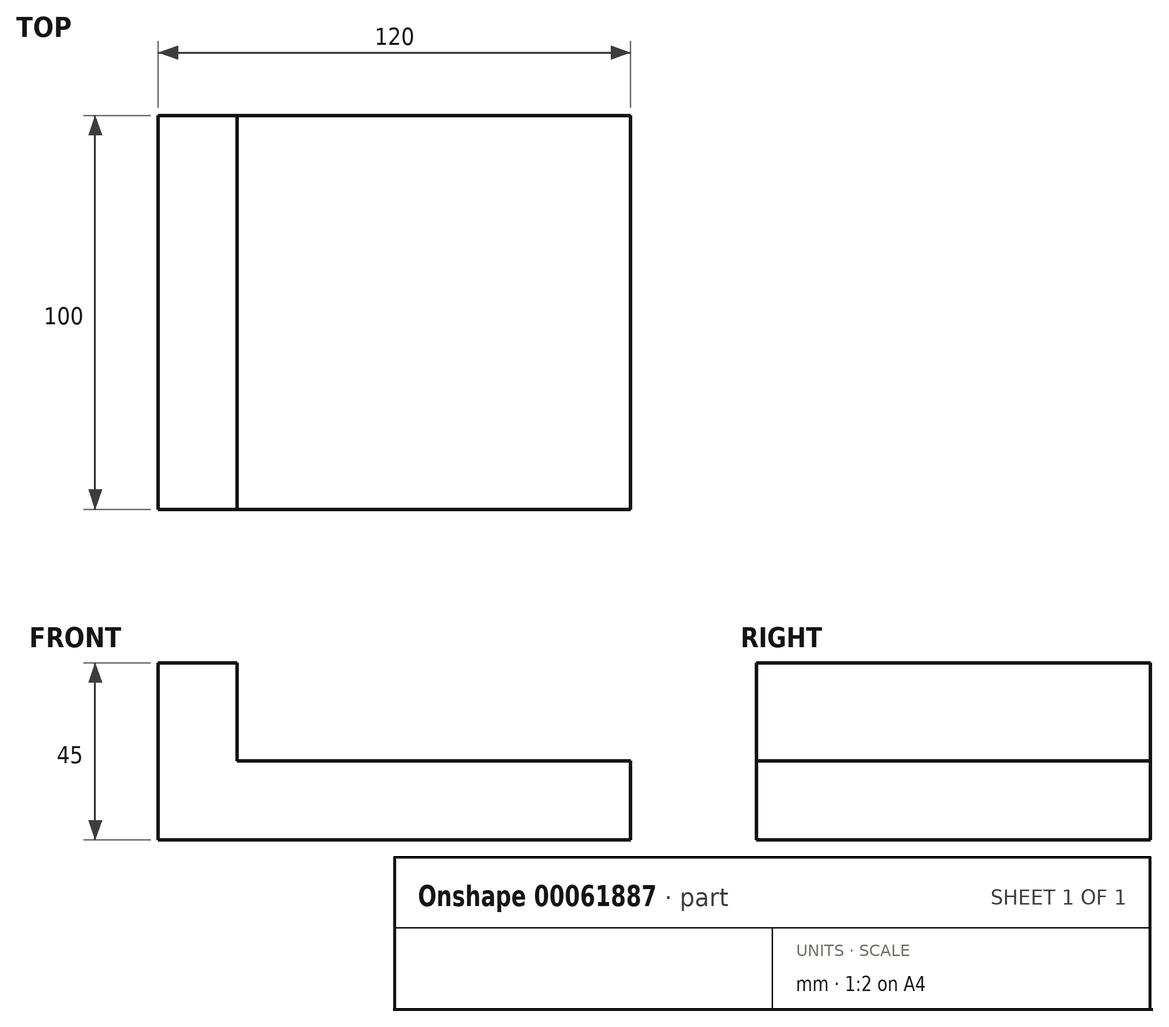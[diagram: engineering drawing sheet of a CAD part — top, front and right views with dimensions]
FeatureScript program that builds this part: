
annotation { "Feature Type Name" : "Feature", "Feature Type Description" : "" }
export const myFeature = defineFeature(function(context is Context, id is Id, definition is map)
    precondition{}
    {
        {
            var Q0;
            Q0=qCreatedBy(makeId("Front.planeOp"),FACE);
            var sketch = newSketch(context, id + "F0", { "sketchPlane" : qUnion([Q0])});
            skLineSegment(sketch, "E0", {"start": v(0, 0) * mm, "end": v(0, 25) * mm});
            skLineSegment(sketch, "E1", {"start": v(0, 0) * mm, "end": v(100, 0) * mm});
            skLineSegment(sketch, "E2", {"start": v(100, 0) * mm, "end": v(100, -20) * mm});
            skLineSegment(sketch, "E3", {"start": v(100, -20) * mm, "end": v(-20, -20) * mm});
            skLineSegment(sketch, "E4", {"start": v(0, 25) * mm, "end": v(-20, 25) * mm});
            skLineSegment(sketch, "E5", {"start": v(-20, 25) * mm, "end": v(-20, -20) * mm});
            skSolve(sketch);
        }
        {
            var Q0;
            Q0=qSketchRegion(id+"F0",true);
            extrude(context, id + "F1", {"entities" : qUnion([Q0]), "endBound" : BoundingType.SYMMETRIC, "depth" : 100 * mm});
        }
    });
